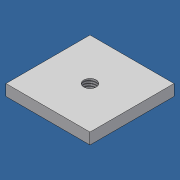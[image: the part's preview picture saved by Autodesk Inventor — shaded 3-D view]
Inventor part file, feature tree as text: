
AUTODESK INVENTOR PART (.ipt)
format: ipt  version: 2012 (Build 160160000, 160)  size: 75,776 bytes
history: native  units: mm (DEFAULTED — no unit token found)
features: sketch x2, extrude x1, hole x1
ambient origin geometry x8: Origin, YZ Plane, XZ Plane, XY Plane, X Axis, Y Axis, Z Axis, Center Point
bodies: Solid1 (feature_tree)
feature tree (4):
  extrude  "Extrusion1"  Depth=6.0mm
  hole  "Hole2"  [1 undecoded]
  sketch  "Sketch1"  dims[d6=45.0mm d7=0.0mm d25=6.0mm]
  sketch  "Sketch5"  dims[d26=45.0mm d27=22.5mm d28=22.5mm d29=6.6548mm d30=19.05mm d31=9.525mm d32=6.35mm d33=14.3117mm d34=25.4mm d35=20.594885mm]
note: 1 required parameter value undecoded (feature->parameter linkage not recoverable at this tier; creation-order binding heuristic only, values carry confidence <= 0.55)
